# Revit family: Drain_Floor_16_Inch_Zurn-Z662_Heavy-Duty
name_source: partatom
category: Plumbing Fixtures
units: mm (PartAtom-declared; Revit-internal decimal feet)

## family parameters
Always vertical = Yes
Cut with Voids When Loaded = No
Maintain Annotation Orientation = No
OmniClass Number = 23.70.50.21.24.14
OmniClass Title = Deck Waste Water Drains
Part Type = Normal
Room Calculation Point = No
Round Connector Dimension = Use Radius
Shared = No
Work Plane-Based = No

## types (27) — shared parameters
Assembly Code = D2030300
CW Connection = No
Default Elevation = 0' - 0"
Description = 16 inch Heavy-Duty Drain
HW Connection = No
Main Material = Iron - Zurn - Cast - Painted - Blue
Manufacturer = Zurn Water, LLC
Manufacurer Brand = Zurn
Model = Z662
Modified Date = July 31, 2025
Product Documentation Link = https://files.zurn.com
Product Page URL = https://www.zurn.com
Product data url = https://bimobject.com
URL = www.zurn.com
Vent Connection = No
Waste Connection = Yes

## per-type parameters (varying)
| type | Approx. Weight (Lbs) | E_Body Height | Flange | Frame Height | Length | Outlet Outer Radius | Outlet Radius | Type Comments | Veneer Frame and Grate | Width |
| ZN662-4NL Outlet |  | 0' - 7 13/16" | 0' - 1 1/16" | 0' - 3 9/16" | 1' - 4 11/16" | 0' - 2 1/2" | 0' - 2" | ZN662-4NL (Neo-Loc Outlet) | Bronze - Zurn - Polished Nickel | 1' - 4 11/16" |
| ZN662-6IP Outlet |  | 0' - 6 5/16" | 0' - 1 1/16" | 0' - 3 9/16" | 1' - 4 11/16" | 0' - 3 5/8" | 0' - 3" | ZN662-6IP (Threaded Outlet) | Bronze - Zurn - Polished Nickel | 1' - 4 11/16" |
| ZN662-4IP Outlet |  | 0' - 6 5/16" | 0' - 1 1/16" | 0' - 3 9/16" | 1' - 4 11/16" | 0' - 2 9/16" | 0' - 2" | ZN662-4IP (Threaded Outlet) | Bronze - Zurn - Polished Nickel | 1' - 4 11/16" |
| ZN662-6IC Outlet |  | 0' - 7 3/4" | 0' - 1 1/16" | 0' - 3 9/16" | 1' - 4 11/16" | 0' - 3 5/8" | 0' - 3" | ZN662-6IC (Inside Caulk Outlet) | Bronze - Zurn - Polished Nickel | 1' - 4 11/16" |
| ZN662-4IC Outlet |  | 0' - 7 3/4" | 0' - 1 1/16" | 0' - 3 9/16" | 1' - 4 11/16" | 0' - 2 5/8" | 0' - 2" | ZN662-4IC (Inside Caulk Outlet) | Bronze - Zurn - Polished Nickel | 1' - 4 11/16" |
| ZN662-6NH Outlet |  | 0' - 7 13/16" | 0' - 1 1/16" | 0' - 3 9/16" | 1' - 4 11/16" | 0' - 3 3/16" | 0' - 3" | ZN662-6NH (No-Hub Outlet) | Bronze - Zurn - Polished Nickel | 1' - 4 11/16" |
| ZN662-4NH Outlet |  | 0' - 7 13/16" | 0' - 1 1/16" | 0' - 3 9/16" | 1' - 4 11/16" | 0' - 2 1/4" | 0' - 2" | ZN662-4NH (No-Hub Outlet) | Bronze - Zurn - Polished Nickel | 1' - 4 11/16" |
| ZN662-3NH Outlet |  | 0' - 7 13/16" | 0' - 1 1/16" | 0' - 3 9/16" | 1' - 4 11/16" | 0' - 1 3/4" | 0' - 1 1/2" | ZB662-3NH (No-Hub Outlet) | Bronze - Zurn - Polished Nickel | 1' - 4 11/16" |
| ZB662-4IC Outlet |  | 0' - 7 3/4" | 0' - 1 1/16" | 0' - 3 9/16" | 1' - 4 11/16" | 0' - 2 5/8" | 0' - 2" | ZB662-4IC (Inside Caulk Outlet) | Bronze - Zurn | 1' - 4 11/16" |
| ZB662-6IP Outlet |  | 0' - 6 5/16" | 0' - 1 1/16" | 0' - 3 9/16" | 1' - 4 11/16" | 0' - 3 5/8" | 0' - 3" | ZB662-6IP (Threaded Outlet) | Bronze - Zurn | 1' - 4 11/16" |
| ZB662-4IP Outlet |  | 0' - 6 5/16" | 0' - 1 1/16" | 0' - 3 9/16" | 1' - 4 11/16" | 0' - 2 9/16" | 0' - 2" | ZB662-4IP (Threaded Outlet) | Bronze - Zurn | 1' - 4 11/16" |
| ZB662-6IC Outlet |  | 0' - 7 3/4" | 0' - 1 1/16" | 0' - 3 9/16" | 1' - 4 11/16" | 0' - 3 5/8" | 0' - 3" | ZB662-6IC (Inside Caulk Outlet) | Bronze - Zurn | 1' - 4 11/16" |
| ZB662-6NH Outlet |  | 0' - 7 13/16" | 0' - 1 1/16" | 0' - 3 9/16" | 1' - 4 11/16" | 0' - 3 3/16" | 0' - 3" | ZB662-6NH (No-Hub Outlet) | Bronze - Zurn | 1' - 4 11/16" |
| ZB662-4NH Outlet |  | 0' - 7 13/16" | 0' - 1 1/16" | 0' - 3 9/16" | 1' - 4 11/16" | 0' - 2 1/4" | 0' - 2" | ZB662-4NH (No-Hub Outlet) | Bronze - Zurn | 1' - 4 11/16" |
| ZB662-4NL Outlet |  | 0' - 7 3/16" | 0' - 1 1/16" | 0' - 3 9/16" | 1' - 4 11/16" | 0' - 2 1/2" | 0' - 2" | ZB662-4NL (Neo-Loc Outlet) | Bronze - Zurn | 1' - 4 11/16" |
| Z662-6IP Outlet | 98 | 0' - 6 5/16" | 0' - 0 3/8" | 0' - 3 3/8" | 1' - 4" | 0' - 3 5/8" | 0' - 3" | Z662-6IP (Threaded) | Iron - Zurn - Cast - Painted - Blue | 1' - 4" |
| Z662-4IP Outlet | 95 | 0' - 6 5/16" | 0' - 0 3/8" | 0' - 3 3/8" | 1' - 4" | 0' - 2 9/16" | 0' - 2" | Z662-4IP (Threaded) | Iron - Zurn - Cast - Painted - Blue | 1' - 4" |
| Z662-6IC Outlet | 98 | 0' - 7 3/4" | 0' - 0 3/8" | 0' - 3 3/8" | 1' - 4" | 0' - 3 5/8" | 0' - 3" | Z662-6IC (Inside Caulk) | Iron - Zurn - Cast - Painted - Blue | 1' - 4" |
| Z662-4IC Outlet | 95 | 0' - 7 3/4" | 0' - 0 3/8" | 0' - 3 3/8" | 1' - 4" | 0' - 2 5/8" | 0' - 2" | Z662-4IC (Inside Caulk Outlet) | Iron - Zurn - Cast - Painted - Blue | 1' - 4" |
| Z662-4NL Outlet | 95 | 0' - 7 3/16" | 0' - 0 3/8" | 0' - 3 3/8" | 1' - 4" | 0' - 2 1/2" | 0' - 2" | Z662-4NL (Neo-Loc Outlet) | Iron - Zurn - Cast - Painted - Blue | 1' - 4" |
| Z662-6NH Outlet | 98 | 0' - 7 13/16" | 0' - 0 3/8" | 0' - 3 3/8" | 1' - 4" | 0' - 3 3/16" | 0' - 3" | Z662-6NH (No-Hub Outlet) | Iron - Zurn - Cast - Painted - Blue | 1' - 4" |
| Z662-4NH Outlet | 95 | 0' - 7 13/16" | 0' - 0 3/8" | 0' - 3 3/8" | 1' - 4" | 0' - 2 1/4" | 0' - 2" | Z662-4NH (No-Hub Outlet) | Iron - Zurn - Cast - Painted - Blue | 1' - 4" |
| ZB662-3NH Outlet | 95 | 0' - 7 13/16" | 0' - 1 1/16" | 0' - 3 9/16" | 1' - 4 11/16" | 0' - 1 3/4" | 0' - 1 1/2" | ZB662-3NH (No-Hub Outlet) | Bronze - Zurn | 1' - 4 11/16" |
| Z662-3NH Outlet | 95 | 0' - 7 13/16" | 0' - 0 3/8" | 0' - 3 3/8" | 1' - 4" | 0' - 1 3/4" | 0' - 1 1/2" | Z662-3NH (No-Hub Outlet) | Iron - Zurn - Cast - Painted - Blue | 1' - 4" |
| ZN662-3NL Outlet | 95 | 0' - 7 3/16" | 0' - 1 1/16" | 0' - 3 9/16" | 1' - 4 11/16" | 0' - 2" | 0' - 1 1/2" | ZN662-3NL (Neo-Loc Outlet) | Bronze - Zurn - Polished Nickel | 1' - 4 11/16" |
| ZB662-3NL Outlet | 95 | 0' - 7 3/16" | 0' - 1 1/16" | 0' - 3 9/16" | 1' - 4 11/16" | 0' - 2" | 0' - 1 1/2" | ZB662-3NL (Neo-Loc Outlet) | Bronze - Zurn | 1' - 4 11/16" |
| Z662-3NL Outlet | 95 | 0' - 7 3/16" | 0' - 0 3/8" | 0' - 3 3/8" | 1' - 4" | 0' - 2" | 0' - 1 1/2" | Z662-3NL (Neo-Loc Outlet) | Iron - Zurn - Cast - Painted - Blue | 1' - 4" |

## geometry (parser evidence)
native form markers: Sweep x7
no freeform markers — native parametric forms only
